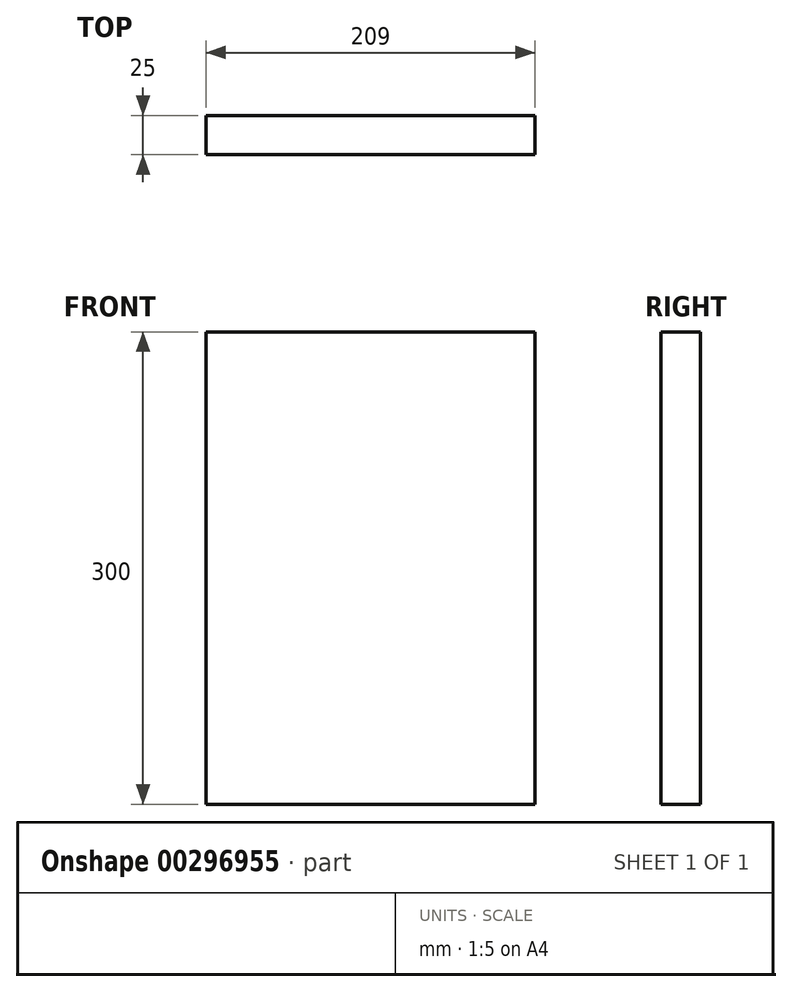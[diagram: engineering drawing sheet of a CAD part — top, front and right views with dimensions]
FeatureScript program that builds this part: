
annotation { "Feature Type Name" : "Feature", "Feature Type Description" : "" }
export const myFeature = defineFeature(function(context is Context, id is Id, definition is map)
    precondition{}
    {
        {
            var Q0;
            Q0=qCreatedBy(makeId("Front.planeOp"),FACE);
            var sketch = newSketch(context, id + "F0", { "sketchPlane" : qUnion([Q0])});
            skLineSegment(sketch, "E0.bottom", {"start": v(0, 0) * mm, "end": v(200, 0) * mm});
            skLineSegment(sketch, "E0.top", {"start": v(0, 300) * mm, "end": v(200, 300) * mm});
            skLineSegment(sketch, "E0.left", {"start": v(0, 0) * mm, "end": v(0, 300) * mm});
            skLineSegment(sketch, "E0.right", {"start": v(200, 0) * mm, "end": v(200, 300) * mm});
            skSolve(sketch);
        }
        {
            var Q0;
            Q0=makeQuery(id+"F0.imprint","IMPRINT",FACE,{"disambiguationData":[TD([[makeQuery(id+"F0.imprint","IMPRINT",EDGE,{"derivedFrom":sQuery(id+"F0.wireOp",EDGE,"E0.bottom")}),1.0]])]});
            extrude(context, id + "F1", {"entities" : qUnion([Q0]), "depth" : 25 * mm});
        }
        {
            var Q0;
            Q0=makeQuery(id+"F1.opExtrude","SWEPT_FACE",FACE,{"disambiguationData":[OSD([sQuery(id+"F0.wireOp",EDGE,"E0.left")])]});
            extrude(context, id + "F2", {"entities" : qUnion([Q0]), "operationType" : NewBodyOperationType.ADD, "depth" : 9 * mm});
        }
    });
